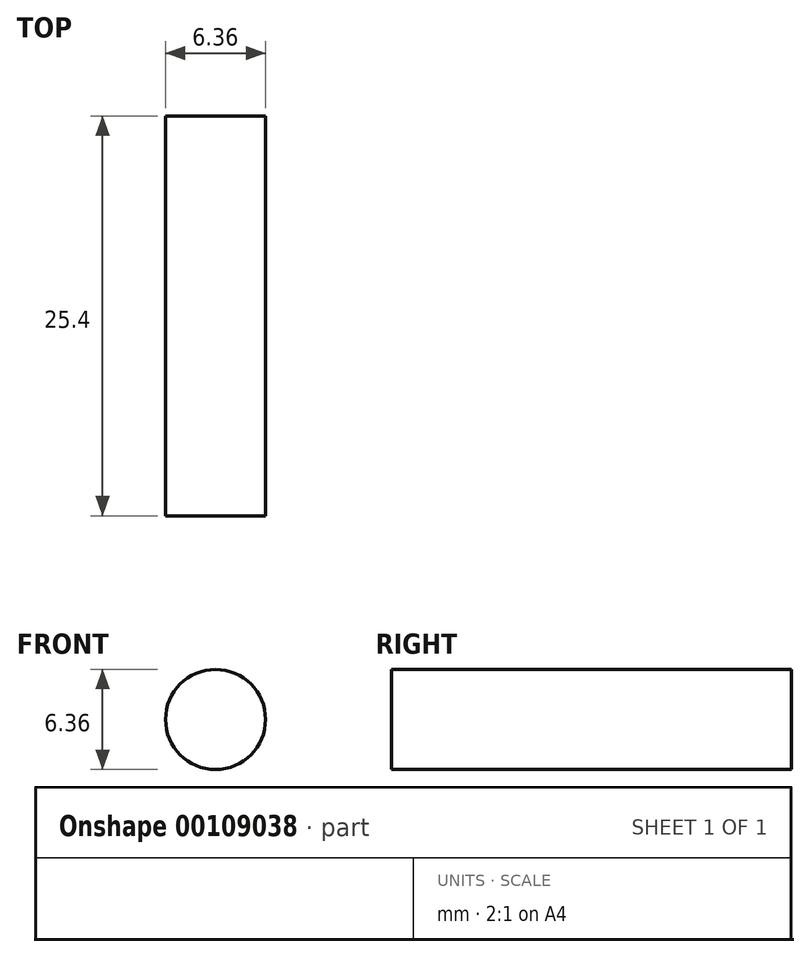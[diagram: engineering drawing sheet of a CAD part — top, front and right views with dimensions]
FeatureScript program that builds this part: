
annotation { "Feature Type Name" : "Feature", "Feature Type Description" : "" }
export const myFeature = defineFeature(function(context is Context, id is Id, definition is map)
    precondition{}
    {
        {
            var Q0;
            Q0=qCreatedBy(makeId("Front.planeOp"),FACE);
            var sketch = newSketch(context, id + "F0", { "sketchPlane" : qUnion([Q0])});
            skCircle(sketch, "E0", {"center": v(0, 0) * mm, "radius": 3.17 * mm});
            skSolve(sketch);
        }
        {
            var Q0;
            Q0=makeQuery(id+"F0.imprint","IMPRINT",FACE,{"disambiguationData":[TD([[makeQuery(id+"F0.imprint","IMPRINT",EDGE,{"derivedFrom":sQuery(id+"F0.wireOp",EDGE,"E0")}),1.0]])]});
            extrude(context, id + "F1", {"entities" : qUnion([Q0]), "depth" : 25.4 * mm});
        }
    });
